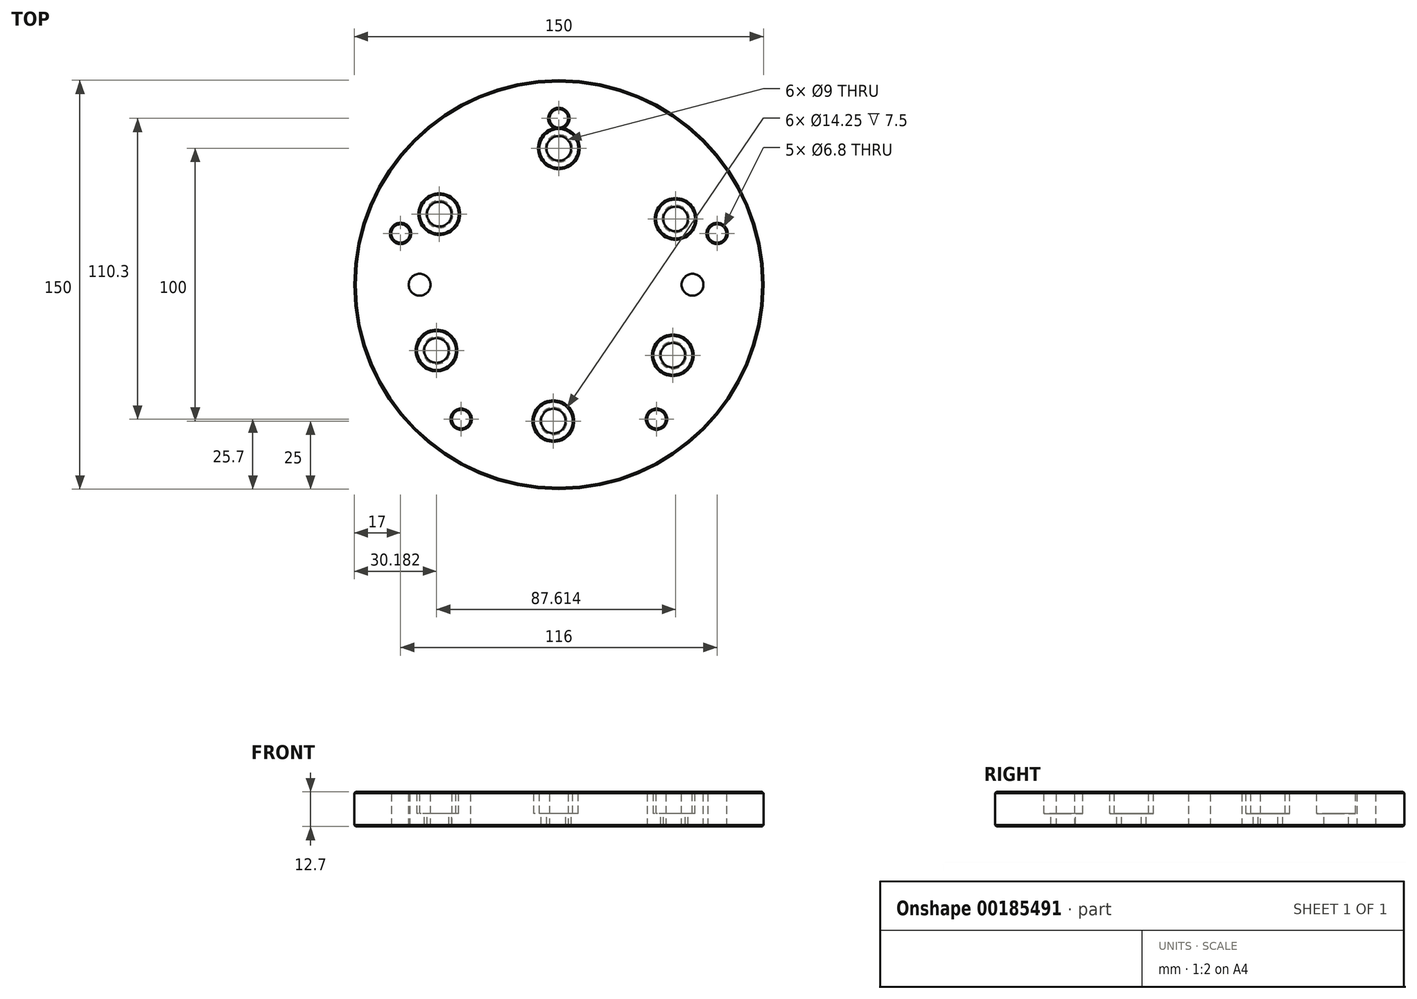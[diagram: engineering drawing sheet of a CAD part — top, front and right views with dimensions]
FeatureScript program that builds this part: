
annotation { "Feature Type Name" : "Feature", "Feature Type Description" : "" }
export const myFeature = defineFeature(function(context is Context, id is Id, definition is map)
    precondition{}
    {
        {
            var Q0;
            Q0=qCreatedBy(makeId("Top.planeOp"),FACE);
            var sketch = newSketch(context, id + "F0", { "sketchPlane" : qUnion([Q0])});
            skCircle(sketch, "E0", {"center": v(0, 0) * mm, "radius": 75 * mm});
            skPoint(sketch, "E1", {"position": v(0, 61) * mm});
            skPoint(sketch, "E2", {"position": v(58, 18.8) * mm});
            skPoint(sketch, "E3", {"position": v(-58, 18.8) * mm});
            skPoint(sketch, "E4", {"position": v(-35.8, -49.3) * mm});
            skPoint(sketch, "E5", {"position": v(35.8, -49.3) * mm});
            skSolve(sketch);
        }
        {
            var Q0;
            Q0=makeQuery(id+"F0.imprint","IMPRINT",FACE,{"disambiguationData":[TD([[makeQuery(id+"F0.imprint","IMPRINT",EDGE,{"derivedFrom":sQuery(id+"F0.wireOp",EDGE,"E0")}),1.0]])]});
            extrude(context, id + "F1", {"entities" : qUnion([Q0]), "depth" : 12.7 * mm});
        }
        {
            var Q0;
            Q0=sQuery(id+"F0.wireOp",VERTEX,"E3");
            var Q1;
            Q1=sQuery(id+"F0.wireOp",VERTEX,"E1");
            var Q2;
            Q2=sQuery(id+"F0.wireOp",VERTEX,"E2");
            var Q3;
            Q3=sQuery(id+"F0.wireOp",VERTEX,"E5");
            var Q4;
            Q4=sQuery(id+"F0.wireOp",VERTEX,"E4");
            var Q5;
            Q5=makeQuery(id+"F1.opExtrude","SWEPT_BODY",BODY,{"disambiguationData":[OSD([sQuery(id+"F0.wireOp",EDGE,"E0")])]});
            hole(context, id + "F2", {"style" : HoleStyle.SIMPLE, "endStyle" : HoleEndStyle.THROUGH, "oppositeDirection" : true, "standardTappedOrClearance" : lookupTablePath({ "standard" : "ISO", "engagement" : "75%", "pitch" : "1.25 mm", "size" : "M8", "type" : "Tapped" }), "standardBlindInLast" : lookupTablePath({ "standard" : "ISO", "engagement" : "75%", "pitch" : "1.25 mm", "size" : "M8", "type" : "Tapped" }), "holeDiameter" : 6.8 * mm, "startFromSketch" : true, "locations" : qUnion([Q0, Q1, Q2, Q3, Q4]), "scope" : qUnion([Q5]), "isTappedThrough" : true, "majorDiameter" : 8 * mm, "showTappedDepth" : true});
        }
        {
            var Q0;
            Q0=makeQuery(id+"F1.opExtrude","CAP_FACE",FACE,{"disambiguationData":[OSD([sQuery(id+"F0.wireOp",EDGE,"E0")])],"isStart":false});
            var sketch = newSketch(context, id + "F3", { "sketchPlane" : qUnion([Q0])});
            skPoint(sketch, "E6", {"position": v(0, 50) * mm});
            skPoint(sketch, "E7.1.0", {"position": v(-43.8, 25.88) * mm});
            skPoint(sketch, "E7.2.0", {"position": v(-44.82, -24.12) * mm});
            skPoint(sketch, "E7.3.0", {"position": v(-2.02, -50) * mm});
            skPoint(sketch, "E7.4.0", {"position": v(41.78, -25.88) * mm});
            skPoint(sketch, "E7.5.0", {"position": v(42.8, 24.12) * mm});
            skPoint(sketch, "E7.center", {"position": v(-1.01, 0) * mm});
            skPoint(sketch, "E8", {"position": v(-51.01, 0) * mm});
            skPoint(sketch, "E9", {"position": v(48.99, 0) * mm});
            skSolve(sketch);
        }
        {
            var Q0;
            Q0=sQuery(id+"F3.wireOp",VERTEX,"E6");
            var Q1;
            Q1=sQuery(id+"F3.wireOp",VERTEX,"E7.1.0");
            var Q2;
            Q2=sQuery(id+"F3.wireOp",VERTEX,"E7.5.0");
            var Q3;
            Q3=sQuery(id+"F3.wireOp",VERTEX,"E7.2.0");
            var Q4;
            Q4=sQuery(id+"F3.wireOp",VERTEX,"E7.3.0");
            var Q5;
            Q5=sQuery(id+"F3.wireOp",VERTEX,"E7.4.0");
            var Q6;
            Q6=makeQuery(id+"F1.opExtrude","SWEPT_BODY",BODY,{"disambiguationData":[OSD([sQuery(id+"F0.wireOp",EDGE,"E0")])]});
            hole(context, id + "F4", {"style" : HoleStyle.C_BORE, "endStyle" : HoleEndStyle.THROUGH, "standardTappedOrClearance" : lookupTablePath({ "fit" : "Normal", "standard" : "ISO", "size" : "M8", "type" : "Clearance" }), "standardBlindInLast" : lookupTablePath({ "fit" : "Normal", "standard" : "ISO", "engagement" : "75%", "pitch" : "1.25 mm", "size" : "M8", "type" : "Clearance & tapped" }), "holeDiameter" : 9 * mm, "cBoreDiameter" : 14.25 * mm, "cBoreDepth" : 8 * mm, "startFromSketch" : true, "locations" : qUnion([Q0, Q1, Q2, Q3, Q4, Q5]), "scope" : qUnion([Q6]), "isTappedThrough" : true, "tappedDepth" : 12 * mm, "tapClearance" : 3, "majorDiameter" : 6 * mm});
        }
        {
            var Q0;
            Q0=makeQuery(id+"F1.opExtrude","CAP_FACE",FACE,{"disambiguationData":[OSD([sQuery(id+"F0.wireOp",EDGE,"E0")])],"isStart":false});
            var Q1;
            Q1=makeQuery(id+"F1.opExtrude","CAP_FACE",FACE,{"disambiguationData":[OSD([sQuery(id+"F0.wireOp",EDGE,"E0")])],"isStart":true});
            chamfer(context, id + "F5", {"entities" : qUnion([Q0, Q1]), "width" : .5 * mm, "tangentPropagation" : true});
        }
        {
            var Q0;
            Q0=sQuery(id+"F3.wireOp",VERTEX,"E8");
            var Q1;
            Q1=sQuery(id+"F3.wireOp",VERTEX,"E9");
            var Q2;
            Q2=makeQuery(id+"F1.opExtrude","SWEPT_BODY",BODY,{"disambiguationData":[OSD([sQuery(id+"F0.wireOp",EDGE,"E0")])]});
            hole(context, id + "F6", {"style" : HoleStyle.SIMPLE, "endStyle" : HoleEndStyle.THROUGH, "standardTappedOrClearance" : lookupTablePath({ "standard" : "ISO", "size" : "8", "type" : "Drilled" }), "standardBlindInLast" : lookupTablePath({ "standard" : "ISO", "size" : "8", "type" : "Drilled" }), "holeDiameter" : 8 * mm, "majorDiameter" : 5 * mm, "isTappedThrough" : true, "tappedDepth" : 12 * mm, "tapClearance" : 3, "startFromSketch" : true, "locations" : qUnion([Q0, Q1]), "scope" : qUnion([Q2])});
        }
    });
